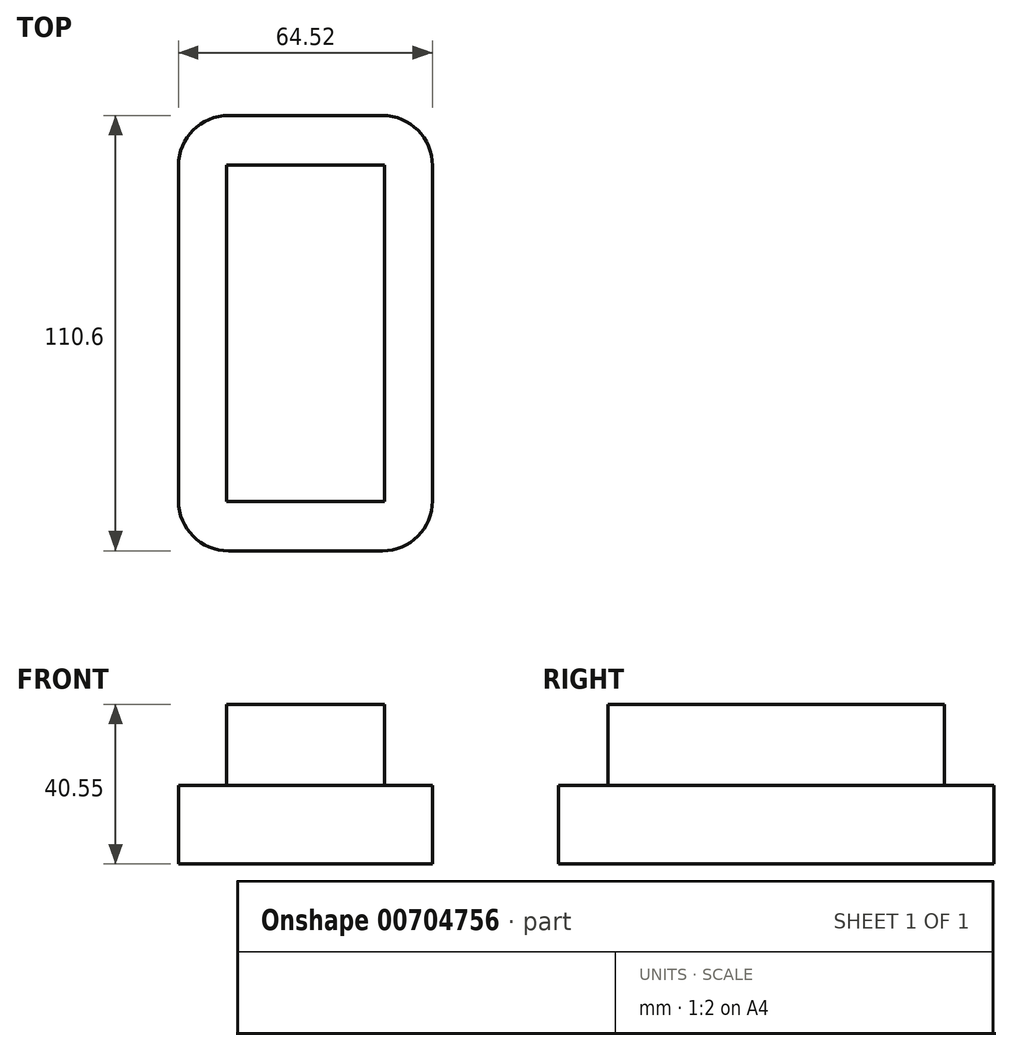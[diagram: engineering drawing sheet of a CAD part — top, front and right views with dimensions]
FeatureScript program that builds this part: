
annotation { "Feature Type Name" : "Feature", "Feature Type Description" : "" }
export const myFeature = defineFeature(function(context is Context, id is Id, definition is map)
    precondition{}
    {
        {
            var Q0;
            Q0=qCreatedBy(makeId("Top.planeOp"),FACE);
            var sketch = newSketch(context, id + "F0", { "sketchPlane" : qUnion([Q0])});
            skLineSegment(sketch, "E0.bottom", {"start": v(-32.26, -55.3) * mm, "end": v(32.26, -55.3) * mm});
            skLineSegment(sketch, "E0.top", {"start": v(-32.26, 55.3) * mm, "end": v(32.26, 55.3) * mm});
            skLineSegment(sketch, "E0.left", {"start": v(-32.26, -55.3) * mm, "end": v(-32.26, 55.3) * mm});
            skLineSegment(sketch, "E0.right", {"start": v(32.26, -55.3) * mm, "end": v(32.26, 55.3) * mm});
            skPoint(sketch, "E0.middle", {"position": v(0, 0) * mm});
            skSolve(sketch);
        }
        {
            var Q0;
            Q0=makeQuery(id+"F0.imprint","IMPRINT",FACE,{"disambiguationData":[TD([[makeQuery(id+"F0.imprint","IMPRINT",EDGE,{"derivedFrom":sQuery(id+"F0.wireOp",EDGE,"E0.bottom")}),1.0]])]});
            extrude(context, id + "F1", {"entities" : qUnion([Q0]), "depth" : 20 * mm, "offsetDistance" : 25.4 * mm});
        }
        {
            var Q0;
            Q0=makeQuery(id+"F1.opExtrude","SWEPT_EDGE",EDGE,{"disambiguationData":[OSD([sQuery(id+"F0.wireOp",EDGE,"E0.top"),sQuery(id+"F0.wireOp",EDGE,"E0.left")])]});
            var Q1;
            Q1=makeQuery(id+"F1.opExtrude","SWEPT_EDGE",EDGE,{"disambiguationData":[OSD([sQuery(id+"F0.wireOp",EDGE,"E0.bottom"),sQuery(id+"F0.wireOp",EDGE,"E0.left")])]});
            var Q2;
            Q2=makeQuery(id+"F1.opExtrude","SWEPT_EDGE",EDGE,{"disambiguationData":[OSD([sQuery(id+"F0.wireOp",EDGE,"E0.top"),sQuery(id+"F0.wireOp",EDGE,"E0.right")])]});
            var Q3;
            Q3=makeQuery(id+"F1.opExtrude","SWEPT_EDGE",EDGE,{"disambiguationData":[OSD([sQuery(id+"F0.wireOp",EDGE,"E0.bottom"),sQuery(id+"F0.wireOp",EDGE,"E0.right")])]});
            fillet(context, id + "F2", {"entities" : qUnion([Q0, Q1, Q2, Q3]), "radius" : 12.7 * mm, "tangentPropagation" : true, "allowEdgeOverflow" : false});
        }
        {
            var Q0;
            Q0=qCreatedBy(makeId("Top.planeOp"),FACE);
            var sketch = newSketch(context, id + "F3", { "sketchPlane" : qUnion([Q0])});
            skLineSegment(sketch, "E1.bottom", {"start": v(-20.1, -42.74) * mm, "end": v(20.1, -42.74) * mm});
            skLineSegment(sketch, "E1.top", {"start": v(-20.1, 42.74) * mm, "end": v(20.1, 42.74) * mm});
            skLineSegment(sketch, "E1.left", {"start": v(-20.1, -42.74) * mm, "end": v(-20.1, 42.74) * mm});
            skLineSegment(sketch, "E1.right", {"start": v(20.1, -42.74) * mm, "end": v(20.1, 42.74) * mm});
            skPoint(sketch, "E1.middle", {"position": v(0, 0) * mm});
            skSolve(sketch);
        }
        {
            var Q0;
            Q0=makeQuery(id+"F3.imprint","IMPRINT",FACE,{"disambiguationData":[TD([[makeQuery(id+"F3.imprint","IMPRINT",EDGE,{"derivedFrom":sQuery(id+"F3.wireOp",EDGE,"E1.bottom")}),1.0]])]});
            extrude(context, id + "F4", {"entities" : qUnion([Q0]), "operationType" : NewBodyOperationType.ADD, "depth" : 40.55 * mm, "offsetDistance" : 25.4 * mm});
        }
    });
